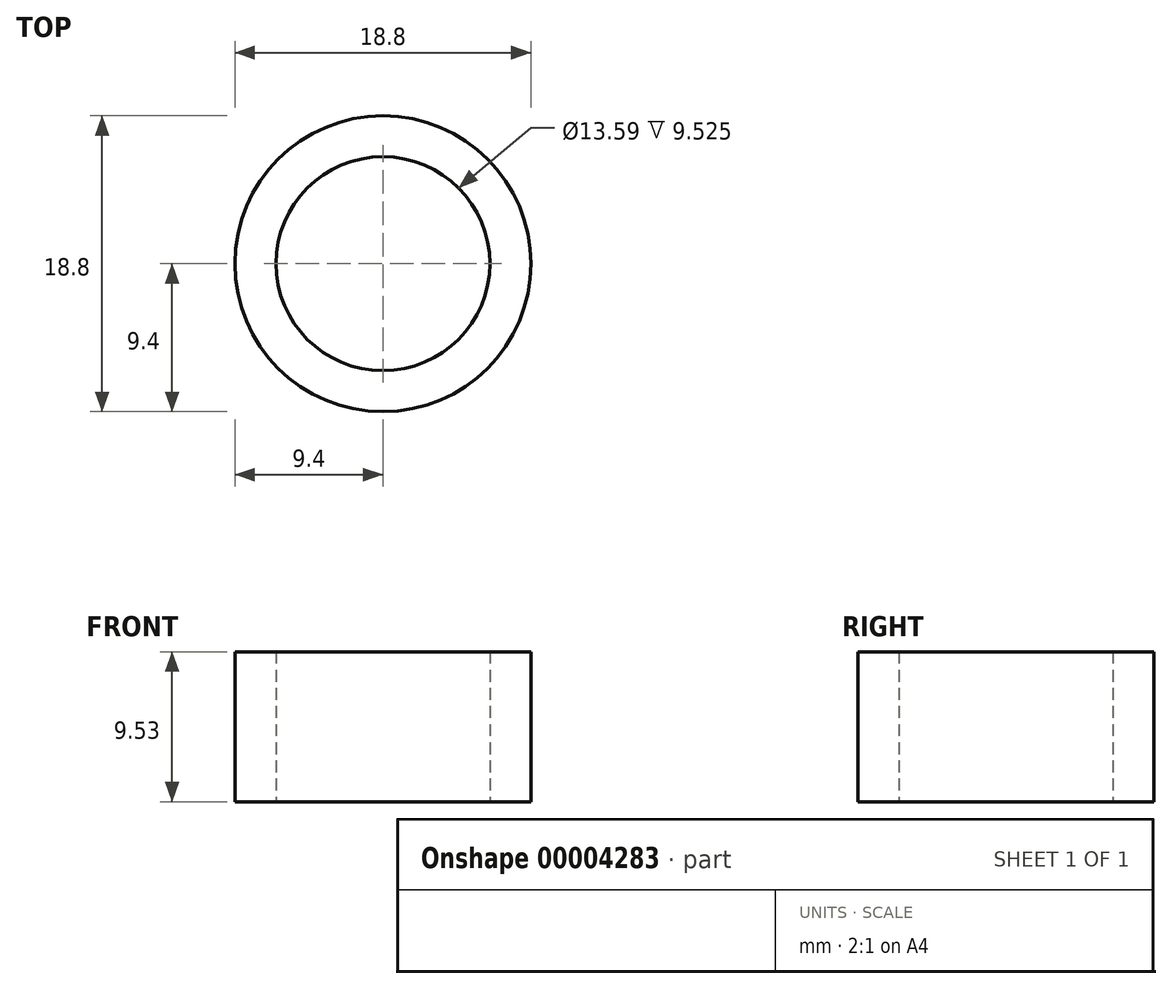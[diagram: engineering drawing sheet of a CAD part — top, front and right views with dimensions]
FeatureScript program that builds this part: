
annotation { "Feature Type Name" : "Feature", "Feature Type Description" : "" }
export const myFeature = defineFeature(function(context is Context, id is Id, definition is map)
    precondition{}
    {
        {
            var Q0;
            Q0=qCreatedBy(makeId("Top.planeOp"),FACE);
            var sketch = newSketch(context, id + "F0", { "sketchPlane" : qUnion([Q0])});
            skCircle(sketch, "E0", {"center": v(0, 0) * mm, "radius": 9.4 * mm});
            skCircle(sketch, "E1", {"center": v(0, 0) * mm, "radius": 6.8 * mm});
            skSolve(sketch);
        }
        {
            var Q0;
            Q0=makeQuery(id+"F0.imprint","IMPRINT",FACE,{"disambiguationData":[TD([[makeQuery(id+"F0.imprint","IMPRINT",EDGE,{"derivedFrom":sQuery(id+"F0.wireOp",EDGE,"E0")}),1.0]])]});
            extrude(context, id + "F1", {"entities" : qUnion([Q0]), "depth" : 9.52 * mm, "offsetDistance" : 25.4 * mm});
        }
    });
